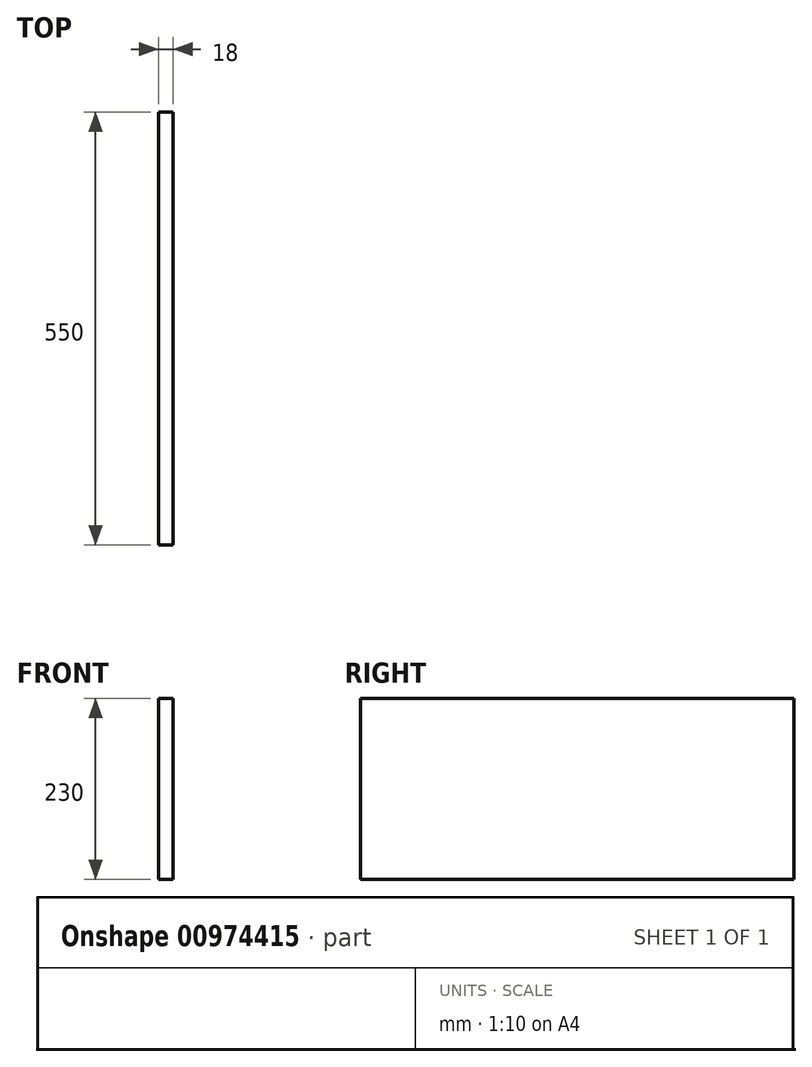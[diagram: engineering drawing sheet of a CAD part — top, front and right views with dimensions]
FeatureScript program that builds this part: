
annotation { "Feature Type Name" : "Feature", "Feature Type Description" : "" }
export const myFeature = defineFeature(function(context is Context, id is Id, definition is map)
    precondition{}
    {
        {
            var Q0;
            Q0=qCreatedBy(makeId("Right.planeOp"),FACE);
            var sketch = newSketch(context, id + "F0", { "sketchPlane" : qUnion([Q0])});
            skLineSegment(sketch, "E0.bottom", {"start": v(275, 115) * mm, "end": v(-275, 115) * mm});
            skLineSegment(sketch, "E0.top", {"start": v(275, -115) * mm, "end": v(-275, -115) * mm});
            skLineSegment(sketch, "E0.left", {"start": v(275, 115) * mm, "end": v(275, -115) * mm});
            skLineSegment(sketch, "E0.right", {"start": v(-275, 115) * mm, "end": v(-275, -115) * mm});
            skPoint(sketch, "E0.middle", {"position": v(0, 0) * mm});
            skSolve(sketch);
        }
        {
            var Q0;
            Q0=makeQuery(id+"F0.imprint","IMPRINT",FACE,{"disambiguationData":[TD([[makeQuery(id+"F0.imprint","IMPRINT",EDGE,{"derivedFrom":sQuery(id+"F0.wireOp",EDGE,"E0.bottom")}),1.0]])]});
            extrude(context, id + "F1", {"entities" : qUnion([Q0]), "depth" : 18 * mm, "offsetDistance" : 25 * mm});
        }
    });
